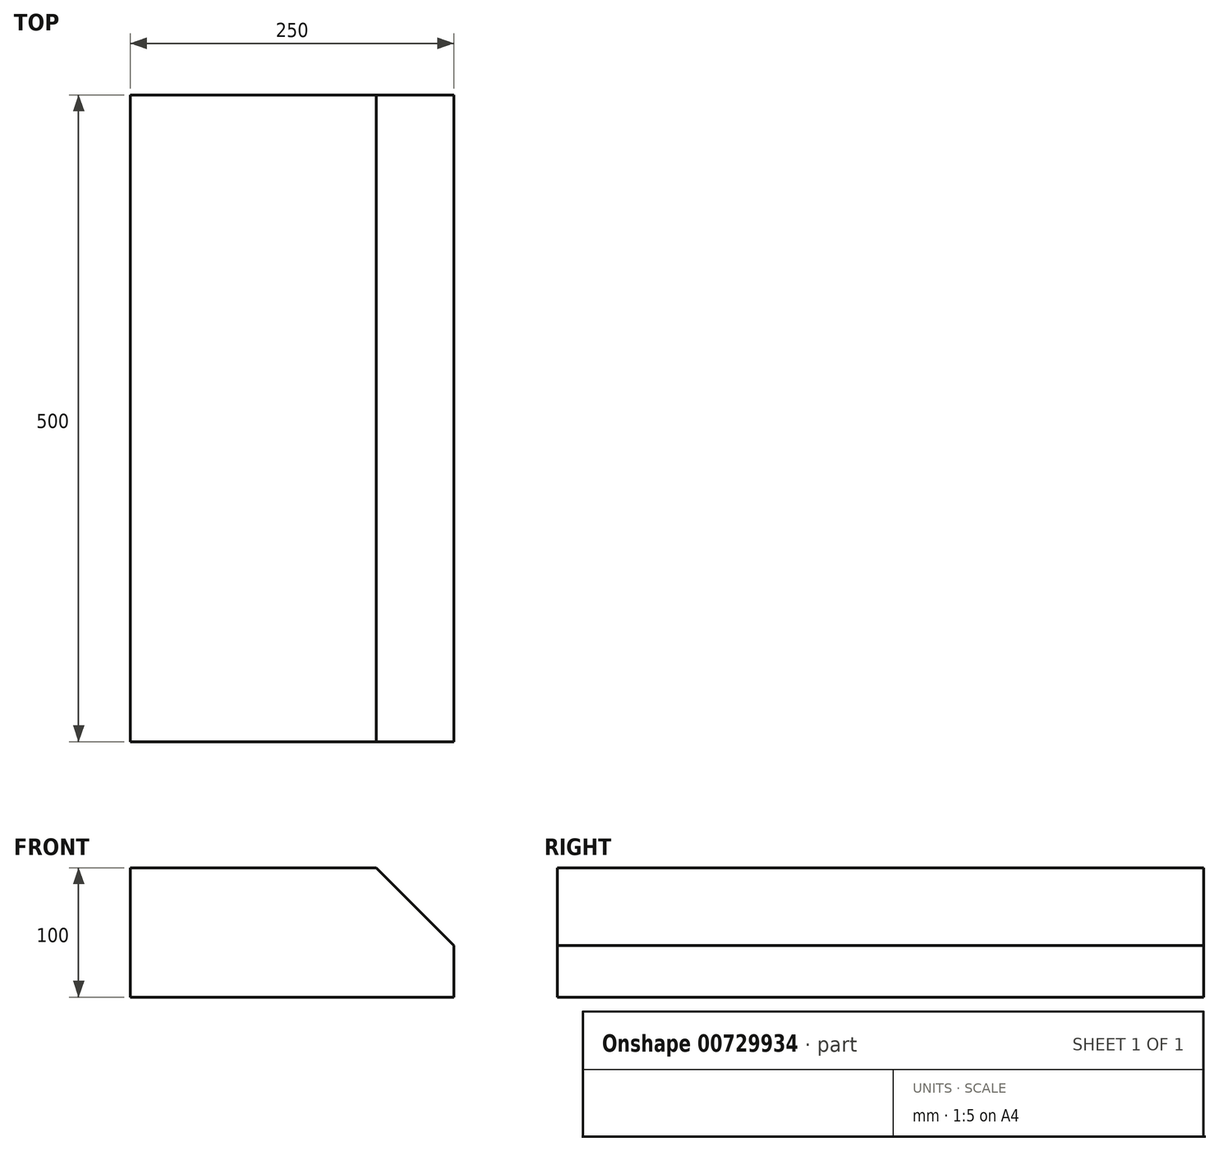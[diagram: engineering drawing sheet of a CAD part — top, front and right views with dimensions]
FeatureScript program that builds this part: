
annotation { "Feature Type Name" : "Feature", "Feature Type Description" : "" }
export const myFeature = defineFeature(function(context is Context, id is Id, definition is map)
    precondition{}
    {
        {
            var Q0;
            Q0=qCreatedBy(makeId("Front.planeOp"),FACE);
            var sketch = newSketch(context, id + "F0", { "sketchPlane" : qUnion([Q0])});
            skLineSegment(sketch, "E0", {"start": v(0, 0) * mm, "end": v(-250, 0) * mm});
            skLineSegment(sketch, "E1", {"start": v(-250, 0) * mm, "end": v(-250, 100) * mm});
            skLineSegment(sketch, "E2", {"start": v(-250, 100) * mm, "end": v(-60, 100) * mm});
            skLineSegment(sketch, "E3", {"start": v(-60, 100) * mm, "end": v(0, 40) * mm});
            skLineSegment(sketch, "E4", {"start": v(0, 40) * mm, "end": v(0, 0) * mm});
            skSolve(sketch);
        }
        {
            var Q0;
            Q0 = qSketchRegion(id + "F0", true);
            extrude(context, id + "F1", {"entities" : qUnion([Q0]), "depth" : 500 * mm, "offsetDistance" : 25 * mm, "symmetric" : true});
        }
    });
